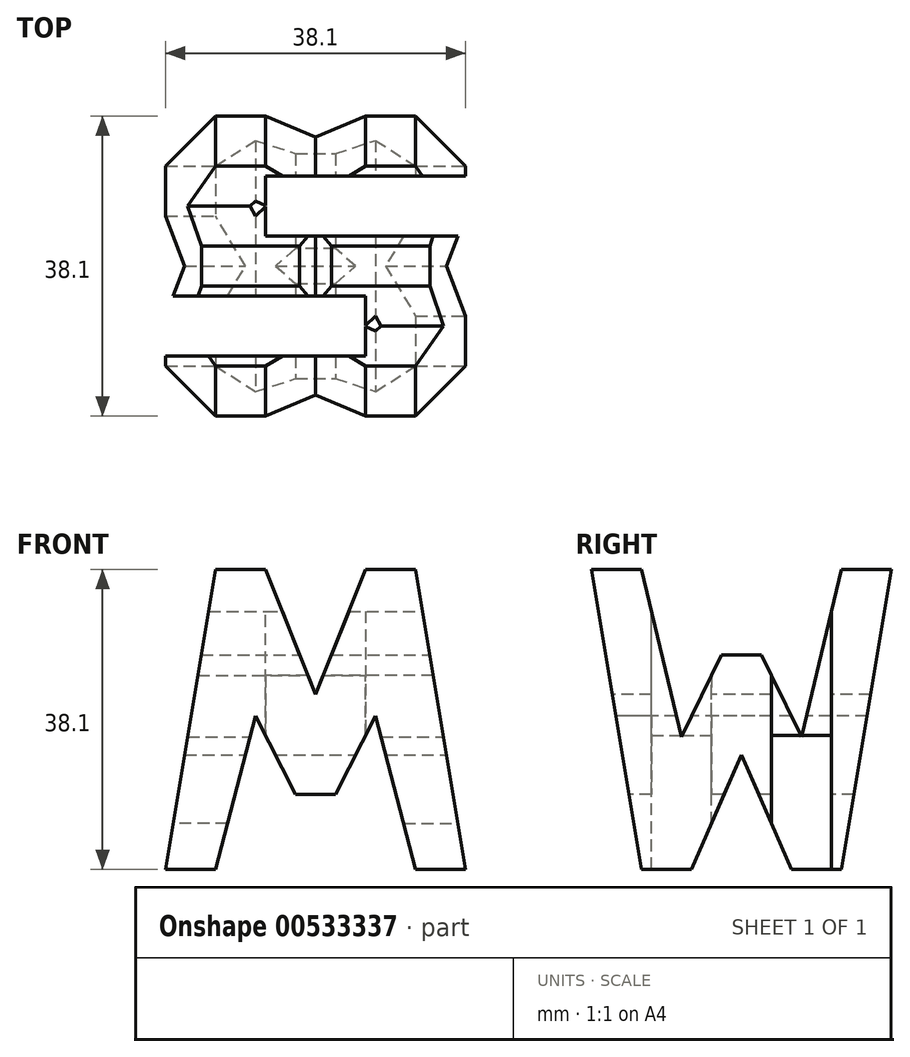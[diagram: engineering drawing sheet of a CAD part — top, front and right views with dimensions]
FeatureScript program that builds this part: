
annotation { "Feature Type Name" : "Feature", "Feature Type Description" : "" }
export const myFeature = defineFeature(function(context is Context, id is Id, definition is map)
    precondition{}
    {
        {
            var Q0;
            Q0=qCreatedBy(makeId("Front.planeOp"),FACE);
            var sketch = newSketch(context, id + "F0", { "sketchPlane" : qUnion([Q0])});
            skLineSegment(sketch, "E0", {"start": v(0, 0) * mm, "end": v(0, 38.1) * mm});
            skLineSegment(sketch, "E1", {"start": v(0, 0) * mm, "end": v(38.1, 0) * mm});
            skLineSegment(sketch, "E2", {"start": v(0, 38.1) * mm, "end": v(38.1, 38.1) * mm});
            skLineSegment(sketch, "E3", {"start": v(38.1, 38.1) * mm, "end": v(38.1, 0) * mm});
            skSolve(sketch);
        }
        {
            var Q0;
            Q0=makeQuery(id+"F0.imprint","IMPRINT",FACE,{"disambiguationData":[TD([[makeQuery(id+"F0.imprint","IMPRINT",EDGE,{"derivedFrom":sQuery(id+"F0.wireOp",EDGE,"E0")}),-1.0]])]});
            extrude(context, id + "F1", {"entities" : qUnion([Q0]), "depth" : 38.1 * mm, "offsetDistance" : 25.4 * mm});
        }
        {
            var Q0;
            Q0=qCreatedBy(makeId("Front.planeOp"),FACE);
            cPlane(context, id + "F2", {"entities" : qUnion([Q0]), "cplaneType" : CPlaneType.OFFSET, "offset" : 38.1 * mm, "width" : 152.4 * mm, "height" : 152.4 * mm});
        }
        {
            var Q0;
            Q0=qCreatedBy(makeId("Right.planeOp"),FACE);
            cPlane(context, id + "F3", {"entities" : qUnion([Q0]), "cplaneType" : CPlaneType.OFFSET, "offset" : 38.1 * mm, "width" : 152.4 * mm, "height" : 152.4 * mm});
        }
        {
            var Q0;
            Q0=qCreatedBy(makeId("Top.planeOp"),FACE);
            cPlane(context, id + "F4", {"entities" : qUnion([Q0]), "cplaneType" : CPlaneType.OFFSET, "offset" : 38.1 * mm, "width" : 152.4 * mm, "height" : 152.4 * mm});
        }
        {
            var Q0;
            Q0=qCreatedBy(id+"F3.planeOp",FACE);
            var sketch = newSketch(context, id + "F5", { "sketchPlane" : qUnion([Q0])});
            skLineSegment(sketch, "E4", {"start": v(-38.1, 38.1) * mm, "end": v(0, 38.1) * mm});
            skLineSegment(sketch, "E5", {"start": v(0, 38.1) * mm, "end": v(0, 0) * mm});
            skLineSegment(sketch, "E6", {"start": v(0, 0) * mm, "end": v(-38.1, 0) * mm});
            skLineSegment(sketch, "E7", {"start": v(-38.1, 0) * mm, "end": v(-38.1, 38.1) * mm});
            skLineSegment(sketch, "E8", {"start": v(-38.1, 38.1) * mm, "end": v(-31.75, 0) * mm});
            skLineSegment(sketch, "E9", {"start": v(-31.75, 38.1) * mm, "end": v(-26.67, 16.85) * mm});
            skLineSegment(sketch, "E10", {"start": v(-11.43, 16.85) * mm, "end": v(-6.35, 38.1) * mm});
            skLineSegment(sketch, "E11", {"start": v(0, 38.1) * mm, "end": v(-6.35, 0) * mm});
            skLineSegment(sketch, "E12", {"start": v(-12.7, 0) * mm, "end": v(-19.05, 14.55) * mm});
            skLineSegment(sketch, "E13", {"start": v(-19.05, 14.55) * mm, "end": v(-25.4, 0) * mm});
            skLineSegment(sketch, "E14", {"start": v(-26.67, 16.85) * mm, "end": v(-21.59, 27.25) * mm});
            skLineSegment(sketch, "E15", {"start": v(-21.59, 27.25) * mm, "end": v(-16.5, 27.25) * mm});
            skLineSegment(sketch, "E16", {"start": v(-16.5, 27.25) * mm, "end": v(-11.43, 16.85) * mm});
            skSolve(sketch);
        }
        {
            var Q0;
            {var subQ1=sQuery(id+"F5.wireOp",EDGE,"E9");Q0=makeQuery(id+"F5.imprint","IMPRINT",FACE,{"disambiguationData":[TD([[makeQuery(id+"F5.imprint","IMPRINT",EDGE,{"derivedFrom":subQ1}),1.0]])]});}
            var Q1;
            {var subQ0=sQuery(id+"F5.wireOp",EDGE,"E7");Q1=makeQuery(id+"F5.imprint","IMPRINT",FACE,{"disambiguationData":[TD([[makeQuery(id+"F5.imprint","IMPRINT",EDGE,{"derivedFrom":subQ0}),-1.0]])]});}
            var Q2;
            {var subQ0=sQuery(id+"F5.wireOp",EDGE,"E12");Q2=makeQuery(id+"F5.imprint","IMPRINT",FACE,{"disambiguationData":[TD([[makeQuery(id+"F5.imprint","IMPRINT",EDGE,{"derivedFrom":subQ0}),1.0]])]});}
            var Q3;
            {var subQ0=sQuery(id+"F5.wireOp",EDGE,"E5");Q3=makeQuery(id+"F5.imprint","IMPRINT",FACE,{"disambiguationData":[TD([[makeQuery(id+"F5.imprint","IMPRINT",EDGE,{"derivedFrom":subQ0}),-1.0]])]});}
            extrude(context, id + "F6", {"entities" : qUnion([Q0, Q1, Q2, Q3]), "operationType" : NewBodyOperationType.REMOVE, "oppositeDirection" : true, "depth" : 38.1 * mm, "offsetDistance" : 25.4 * mm});
        }
        {
            var Q0;
            Q0=qCreatedBy(id+"F2.planeOp",FACE);
            var sketch = newSketch(context, id + "F7", { "sketchPlane" : qUnion([Q0])});
            skLineSegment(sketch, "E17", {"start": v(0, 0) * mm, "end": v(0, 38.1) * mm});
            skLineSegment(sketch, "E18", {"start": v(0, 38.1) * mm, "end": v(38.1, 38.1) * mm});
            skLineSegment(sketch, "E19", {"start": v(38.1, 38.1) * mm, "end": v(38.1, 0) * mm});
            skLineSegment(sketch, "E20", {"start": v(38.1, 0) * mm, "end": v(0, 0) * mm});
            skLineSegment(sketch, "E21", {"start": v(0, 0) * mm, "end": v(6.35, 38.1) * mm});
            skLineSegment(sketch, "E22", {"start": v(6.35, 0) * mm, "end": v(11.43, 19.5) * mm});
            skLineSegment(sketch, "E23", {"start": v(11.43, 19.5) * mm, "end": v(16.51, 9.52) * mm});
            skLineSegment(sketch, "E24", {"start": v(16.51, 9.52) * mm, "end": v(21.6, 9.52) * mm});
            skLineSegment(sketch, "E25", {"start": v(21.6, 9.52) * mm, "end": v(26.67, 19.5) * mm});
            skLineSegment(sketch, "E26", {"start": v(26.67, 19.5) * mm, "end": v(31.75, 0) * mm});
            skLineSegment(sketch, "E27", {"start": v(12.7, 38.1) * mm, "end": v(19.05, 22.23) * mm});
            skLineSegment(sketch, "E28", {"start": v(19.05, 22.23) * mm, "end": v(25.4, 38.1) * mm});
            skLineSegment(sketch, "E29", {"start": v(31.75, 38.1) * mm, "end": v(38.1, 0) * mm});
            skSolve(sketch);
        }
        {
            var Q0;
            {var subQ0=sQuery(id+"F7.wireOp",EDGE,"E27");Q0=makeQuery(id+"F7.imprint","IMPRINT",FACE,{"disambiguationData":[TD([[makeQuery(id+"F7.imprint","IMPRINT",EDGE,{"derivedFrom":subQ0}),1.0]])]});}
            var Q1;
            {var subQ0=sQuery(id+"F7.wireOp",EDGE,"E17");Q1=makeQuery(id+"F7.imprint","IMPRINT",FACE,{"disambiguationData":[TD([[makeQuery(id+"F7.imprint","IMPRINT",EDGE,{"derivedFrom":subQ0}),-1.0]])]});}
            var Q2;
            {var subQ0=sQuery(id+"F7.wireOp",EDGE,"E19");Q2=makeQuery(id+"F7.imprint","IMPRINT",FACE,{"disambiguationData":[TD([[makeQuery(id+"F7.imprint","IMPRINT",EDGE,{"derivedFrom":subQ0}),-1.0]])]});}
            var Q3;
            {var subQ0=sQuery(id+"F7.wireOp",EDGE,"E22");Q3=makeQuery(id+"F7.imprint","IMPRINT",FACE,{"disambiguationData":[TD([[makeQuery(id+"F7.imprint","IMPRINT",EDGE,{"derivedFrom":subQ0}),-1.0]])]});}
            extrude(context, id + "F8", {"entities" : qUnion([Q0, Q1, Q2, Q3]), "operationType" : NewBodyOperationType.REMOVE, "oppositeDirection" : true, "depth" : 38.1 * mm, "offsetDistance" : 25.4 * mm});
        }
        {
            var Q0;
            Q0=qCreatedBy(id+"F4.planeOp",FACE);
            var sketch = newSketch(context, id + "F9", { "sketchPlane" : qUnion([Q0])});
            skLineSegment(sketch, "E30", {"start": v(0, 0) * mm, "end": v(0, -38.1) * mm});
            skLineSegment(sketch, "E31", {"start": v(0, -38.1) * mm, "end": v(38.1, -38.1) * mm});
            skLineSegment(sketch, "E32", {"start": v(38.1, -38.1) * mm, "end": v(38.1, 0) * mm});
            skLineSegment(sketch, "E33", {"start": v(38.1, 0) * mm, "end": v(0, 0) * mm});
            skLineSegment(sketch, "E34", {"start": v(38.1, -7.62) * mm, "end": v(12.7, -7.62) * mm});
            skLineSegment(sketch, "E35", {"start": v(12.7, -7.62) * mm, "end": v(12.7, -15.24) * mm});
            skLineSegment(sketch, "E36", {"start": v(12.7, -15.24) * mm, "end": v(38.1, -15.24) * mm});
            skLineSegment(sketch, "E37", {"start": v(25.4, -22.86) * mm, "end": v(25.4, -30.48) * mm});
            skLineSegment(sketch, "E38", {"start": v(25.4, -30.48) * mm, "end": v(0, -30.48) * mm});
            skLineSegment(sketch, "E39", {"start": v(25.4, -22.86) * mm, "end": v(0, -22.86) * mm});
            skSolve(sketch);
        }
        {
            var Q0;
            {var subQ0=sQuery(id+"F9.wireOp",EDGE,"E34");Q0=makeQuery(id+"F9.imprint","IMPRINT",FACE,{"disambiguationData":[TD([[makeQuery(id+"F9.imprint","IMPRINT",EDGE,{"derivedFrom":subQ0}),1.0]])]});}
            var Q1;
            Q1=makeQuery(id+"F9.imprint","IMPRINT",FACE,{"disambiguationData":[TD([[makeQuery(id+"F9.imprint","IMPRINT",EDGE,{"derivedFrom":sQuery(id+"F9.wireOp",EDGE,"E37")}),-1.0]])]});
            extrude(context, id + "F10", {"entities" : qUnion([Q0, Q1]), "operationType" : NewBodyOperationType.REMOVE, "oppositeDirection" : true, "depth" : 38.1 * mm, "offsetDistance" : 25.4 * mm});
        }
    });
